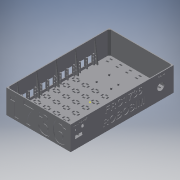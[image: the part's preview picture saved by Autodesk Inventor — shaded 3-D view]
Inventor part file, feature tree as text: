
AUTODESK INVENTOR PART (.ipt)
format: ipt  version: 2016 (Build 200138000, 138)  size: 1,938,944 bytes
history: native  units: in
note: dims shown in document units (in); Inventor stores cm internally (conversion verified against a paired STEP export)
features: extrude x15, sketch x15, chamfer x10
ambient origin geometry x8: Origin, YZ Plane, XZ Plane, XY Plane, X Axis, Y Axis, Z Axis, Center Point
bodies: Solid1 (feature_tree)
feature tree (40):
  extrude  "Extrusion1"  Depth=16.0in
  extrude  "Extrusion2"  Depth=0.2in TaperAngle=0.0deg
  extrude  "Extrusion3"  Depth=3.0in
  chamfer  "Chamfer1"  Distance=3.5in
  chamfer  "Chamfer2"  Distance=0.5in Angle=45.0deg
  chamfer  "Chamfer3"  Distance=0.5in Angle=45.0deg
  chamfer  "Chamfer4"  Distance=0.5in Angle=45.0deg
  chamfer  "Chamfer5"  Distance=0.5in Angle=45.0deg
  chamfer  "Chamfer6"  Distance=0.5in Angle=45.0deg
  chamfer  "Chamfer7"  Distance=0.5in Angle=45.0deg
  chamfer  "Chamfer8"  Distance=0.5in Angle=45.0deg
  chamfer  "Chamfer9"  Distance=0.5in Angle=45.0deg
  extrude  "Extrusion4"  Depth=0.25in TaperAngle=0.0deg
  extrude  "Extrusion6"  Depth=0.075in TaperAngle=0.0deg
  extrude  "Extrusion8"  Depth=0.075in TaperAngle=0.0deg
  extrude  "Extrusion9"  Depth=0.4724in
  extrude  "Extrusion10"  TaperAngle=0.0deg  [1 undecoded]
  extrude  "Extrusion11"  Depth=0.4528in
  extrude  "Extrusion12"  TaperAngle=0.0deg  [1 undecoded]
  extrude  "Extrusion13"  Depth=1.1in
  chamfer  "Chamfer11"  Distance=3.5in Angle=45.0deg
  extrude  "Extrusion14"  Depth=12.0in
  extrude  "Extrusion15"  TaperAngle=0.0deg  [1 undecoded]
  extrude  "Extrusion18"  Depth=3.0in
  sketch  "Sketch21"  dims[d94=1.5748in d96=3.0in d97=0.3937in d99=1.0in d101=0.1969in d102=0.0in d103=1.5748in d105=3.0in d106=0.3937in d108=1.0in d110=1.5in d111=0.0in d117=12.0in d118=0.0in]
  sketch  "Sketch1"  dims[d0=10.0in d1=16.0in]
  sketch  "Sketch2"  dims[d2=2.7559in d4=1.5in d5=2.3622in d7=1.5in]
  sketch  "Sketch3"  dims[d11=2.7559in d13=2.3622in d14=2.3622in d16=1.5in d17=0.3937in d19=1.0in d21=0.2in d22=0.0in]
  sketch  "Sketch8"  dims[d23=3.5in d24=0.0in d25=0.7874in d27=9.343in d28=1.9685in d30=3.0in d33=3.5in d34=0.0in d35=0.5in d36=3.5in d37=45.0deg d38=0.5in d39=3.5in d40=45.0deg d41=0.5in d42=3.5in d43=45.0deg d44=0.5in d45=3.5in d46=45.0deg d47=0.5in d48=3.5in d49=45.0deg d50=0.5in d51=3.5in d52=45.0deg d53=0.5in d54=3.5in d55=45.0deg d56=0.5in d57=3.5in d58=45.0deg]
  sketch  "Sketch9"  dims[d59=0.5in d60=3.5in d61=45.0deg d65=0.25in d66=0.0in]
  sketch  "Sketch10"  dims[d69=0.075in d70=0.0in d72=0.0in d73=0.075in]
  sketch  "Sketch11"  dims[d74=0.075in d75=0.0in d76=0.075in d77=0.0in]
  sketch  "Sketch12"  dims[d78=0.1969in d79=0.4724in]
  sketch  "Sketch13"  dims[d80=0.1969in d81=0.0in]
  sketch  "Sketch14"  dims[d82=1.1811in d83=0.4528in]
  sketch  "Sketch15"  dims[d84=0.1969in d85=0.0in]
  sketch  "Sketch16"  dims[d86=0.075in d87=0.0in d88=1.1in]
  sketch  "Sketch17"  dims[d89=0.1969in]
  sketch  "Sketch20"  dims[d90=0.0in d91=0.49in d92=3.5in d93=45.0deg]
  extrude  "Extrusion7"  Depth=1.5in TaperAngle=0.0deg
note: 3 required parameter values undecoded (feature->parameter linkage not recoverable at this tier; creation-order binding heuristic only, values carry confidence <= 0.55)
